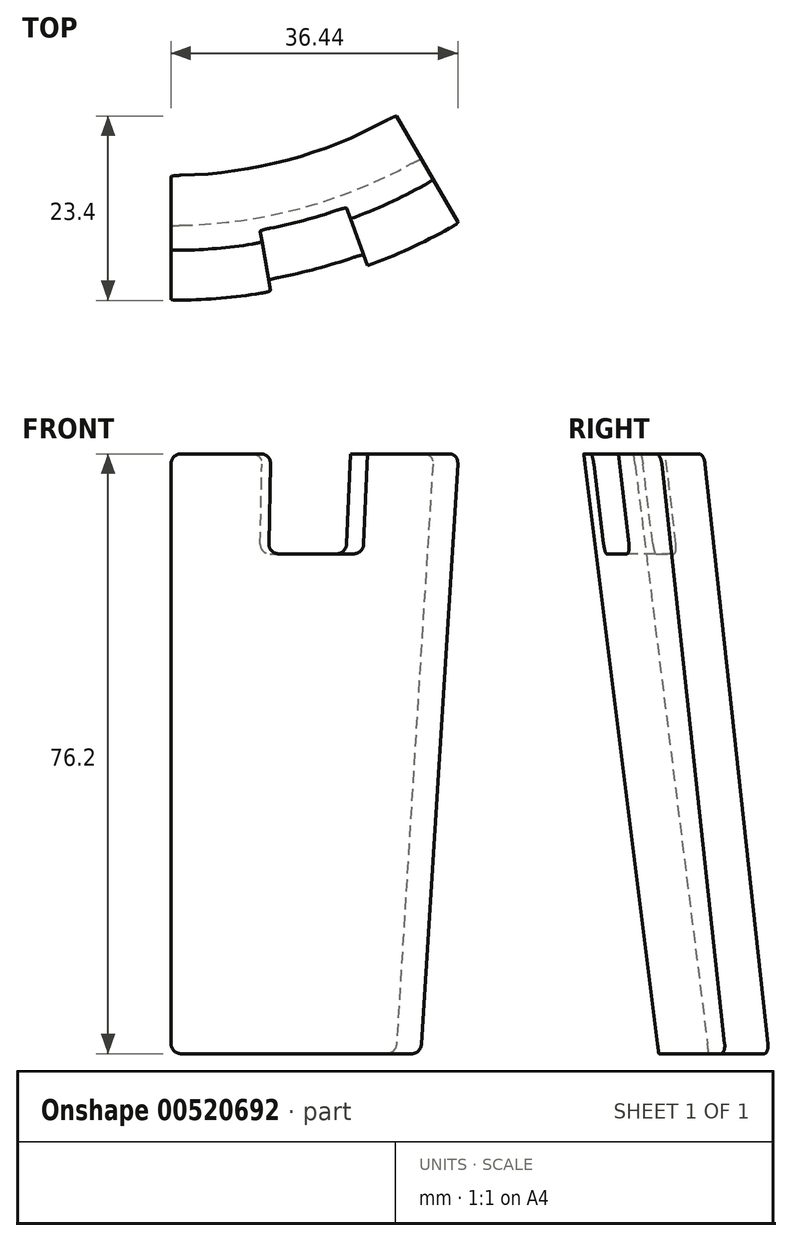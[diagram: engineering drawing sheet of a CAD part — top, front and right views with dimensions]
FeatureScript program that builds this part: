
annotation { "Feature Type Name" : "Feature", "Feature Type Description" : "" }
export const myFeature = defineFeature(function(context is Context, id is Id, definition is map)
    precondition{}
    {
        {
            var Q0;
            Q0=qCreatedBy(makeId("Right.planeOp"),FACE);
            var sketch = newSketch(context, id + "F0", { "sketchPlane" : qUnion([Q0])});
            skLineSegment(sketch, "E0", {"start": v(0, 0) * mm, "end": v(0, 25.4) * mm});
            skLineSegment(sketch, "E1", {"start": v(0, 25.4) * mm, "end": v(0, 50.8) * mm});
            skLineSegment(sketch, "E2", {"start": v(0, 50.8) * mm, "end": v(0, 76.2) * mm});
            skLineSegment(sketch, "E3", {"start": v(0, 76.2) * mm, "end": v(-73.03, 76.2) * mm});
            skLineSegment(sketch, "E4", {"start": v(0, 0) * mm, "end": v(-63.5, 0) * mm});
            skLineSegment(sketch, "E5", {"start": v(-63.5, 0) * mm, "end": v(-66.68, 25.4) * mm});
            skLineSegment(sketch, "E6", {"start": v(-69.85, 50.8) * mm, "end": v(-66.67, 25.4) * mm});
            skLineSegment(sketch, "E7", {"start": v(-69.85, 50.8) * mm, "end": v(-73.03, 76.2) * mm});
            skSolve(sketch);
        }
        {
            var Q0;
            Q0=qCreatedBy(makeId("Top.planeOp"),FACE);
            var sketch = newSketch(context, id + "F1", { "sketchPlane" : qUnion([Q0])});
            skCircle(sketch, "E8", {"center": v(0, 0) * mm, "radius": 63.5 * mm});
            skSolve(sketch);
        }
        {
            var Q0;
            Q0 = qSketchRegion(id + "F0", true);
            var Q1;
            Q1=sQuery(id+"F1.wireOp",EDGE,"E8");
            revolve(context, id + "F2", {"entities" : qUnion([Q0]), "axis" : qUnion([Q1]), "revolveType" : RevolveType.ONE_DIRECTION, "angle" : 30 * degree});
        }
        {
            var Q0;
            Q0=qCreatedBy(makeId("Right.planeOp"),FACE);
            var sketch = newSketch(context, id + "F3", { "sketchPlane" : qUnion([Q0])});
            skLineSegment(sketch, "E9", {"start": v(0, 0) * mm, "end": v(0, 25.4) * mm});
            skLineSegment(sketch, "E10", {"start": v(0, 25.4) * mm, "end": v(0, 50.8) * mm});
            skLineSegment(sketch, "E11", {"start": v(0, 50.8) * mm, "end": v(0, 76.2) * mm});
            skLineSegment(sketch, "E12", {"start": v(0, 76.2) * mm, "end": v(-66.68, 76.2) * mm});
            skLineSegment(sketch, "E13.bottom", {"start": v(0, 0) * mm, "end": v(-57.15, 0) * mm});
            skLineSegment(sketch, "E13.top", {"start": v(0, 0) * mm, "end": v(-57.15, 0) * mm});
            skLineSegment(sketch, "E13.left", {"start": v(0, 0) * mm, "end": v(0, 0) * mm});
            skLineSegment(sketch, "E13.right", {"start": v(-57.15, 0) * mm, "end": v(-57.15, 0) * mm});
            skLineSegment(sketch, "E14", {"start": v(-66.68, 76.2) * mm, "end": v(-57.15, 0) * mm});
            skSolve(sketch);
        }
        {
            var Q0;
            Q0=qCreatedBy(makeId("Top.planeOp"),FACE);
            var sketch = newSketch(context, id + "F4", { "sketchPlane" : qUnion([Q0])});
            skCircle(sketch, "E15", {"center": v(0, 0) * mm, "radius": 57.15 * mm});
            skSolve(sketch);
        }
        {
            var Q0;
            Q0 = qSketchRegion(id + "F3", true);
            var Q1;
            Q1=sQuery(id+"F4.wireOp",EDGE,"E15");
            revolve(context, id + "F5", {"operationType" : NewBodyOperationType.REMOVE, "entities" : qUnion([Q0]), "axis" : qUnion([Q1]), "revolveType" : RevolveType.FULL, "oppositeDirection" : true});
        }
        {
            var Q0;
            Q0=makeQuery(id+"F2.opRevolve","SWEPT_FACE",FACE,{"disambiguationData":[OSD([sQuery(id+"F0.wireOp",EDGE,"E3")])]});
            var sketch = newSketch(context, id + "F6", { "sketchPlane" : qUnion([Q0])});
            skLineSegment(sketch, "E16", {"start": v(0, 0) * mm, "end": v(12.68, -71.92) * mm});
            skLineSegment(sketch, "E17", {"start": v(0, 0) * mm, "end": v(24.98, -68.62) * mm});
            skArc(sketch, "E18", {"start": v(12.68, -71.92) * mm, "mid": v(20.63, -76.98) * mm, "end": v(24.98, -68.62) * mm});
            skSolve(sketch);
        }
        {
            var Q0;
            Q0 = qSketchRegion(id + "F6", true);
            extrude(context, id + "F7", {"entities" : qUnion([Q0]), "operationType" : NewBodyOperationType.REMOVE, "oppositeDirection" : true, "depth" : 12.7 * mm, "offsetDistance" : 25.4 * mm});
        }
        {
            var Q0;
            Q0=makeQuery(id+"F7.boolean.opBoolean","COPY",EDGE,{"derivedFrom":makeQuery(id+"F7.opExtrude","CAP_EDGE",EDGE,{"disambiguationData":[OSD([sQuery(id+"F6.wireOp",EDGE,"E16")])],"isStart":true})});
            var Q1;
            Q1=makeQuery(id+"F7.boolean.opBoolean","COPY",EDGE,{"derivedFrom":makeQuery(id+"F7.opExtrude","CAP_EDGE",EDGE,{"disambiguationData":[OSD([sQuery(id+"F6.wireOp",EDGE,"E17")])],"isStart":true})});
            var Q2;
            Q2=makeQuery(id+"F2.opRevolve","CAP_EDGE",EDGE,{"disambiguationData":[OSD([sQuery(id+"F0.wireOp",EDGE,"E3")])],"isStart":false});
            var Q3;
            Q3=makeQuery(id+"F2.opRevolve","CAP_EDGE",EDGE,{"disambiguationData":[OSD([sQuery(id+"F0.wireOp",EDGE,"E4")])],"isStart":false});
            var Q4;
            Q4=makeQuery(id+"F2.opRevolve","CAP_EDGE",EDGE,{"disambiguationData":[OSD([sQuery(id+"F0.wireOp",EDGE,"E4")])],"isStart":true});
            var Q5;
            Q5=makeQuery(id+"F2.opRevolve","CAP_EDGE",EDGE,{"disambiguationData":[OSD([sQuery(id+"F0.wireOp",EDGE,"E3")])],"isStart":true});
            var Q6;
            Q6=makeQuery(id+"F7.boolean.opBoolean","COPY",EDGE,{"derivedFrom":makeQuery(id+"F7.opExtrude","CAP_EDGE",EDGE,{"disambiguationData":[OSD([sQuery(id+"F6.wireOp",EDGE,"E16")])],"isStart":false})});
            var Q7;
            Q7=makeQuery(id+"F7.boolean.opBoolean","COPY",EDGE,{"derivedFrom":makeQuery(id+"F7.opExtrude","CAP_EDGE",EDGE,{"disambiguationData":[OSD([sQuery(id+"F6.wireOp",EDGE,"E17")])],"isStart":false})});
            fillet(context, id + "F8", {"entities" : qUnion([Q0, Q1, Q2, Q3, Q4, Q5, Q6, Q7]), "radius" : 1.27 * mm, "tangentPropagation" : true, "allowEdgeOverflow" : false});
        }
    });
